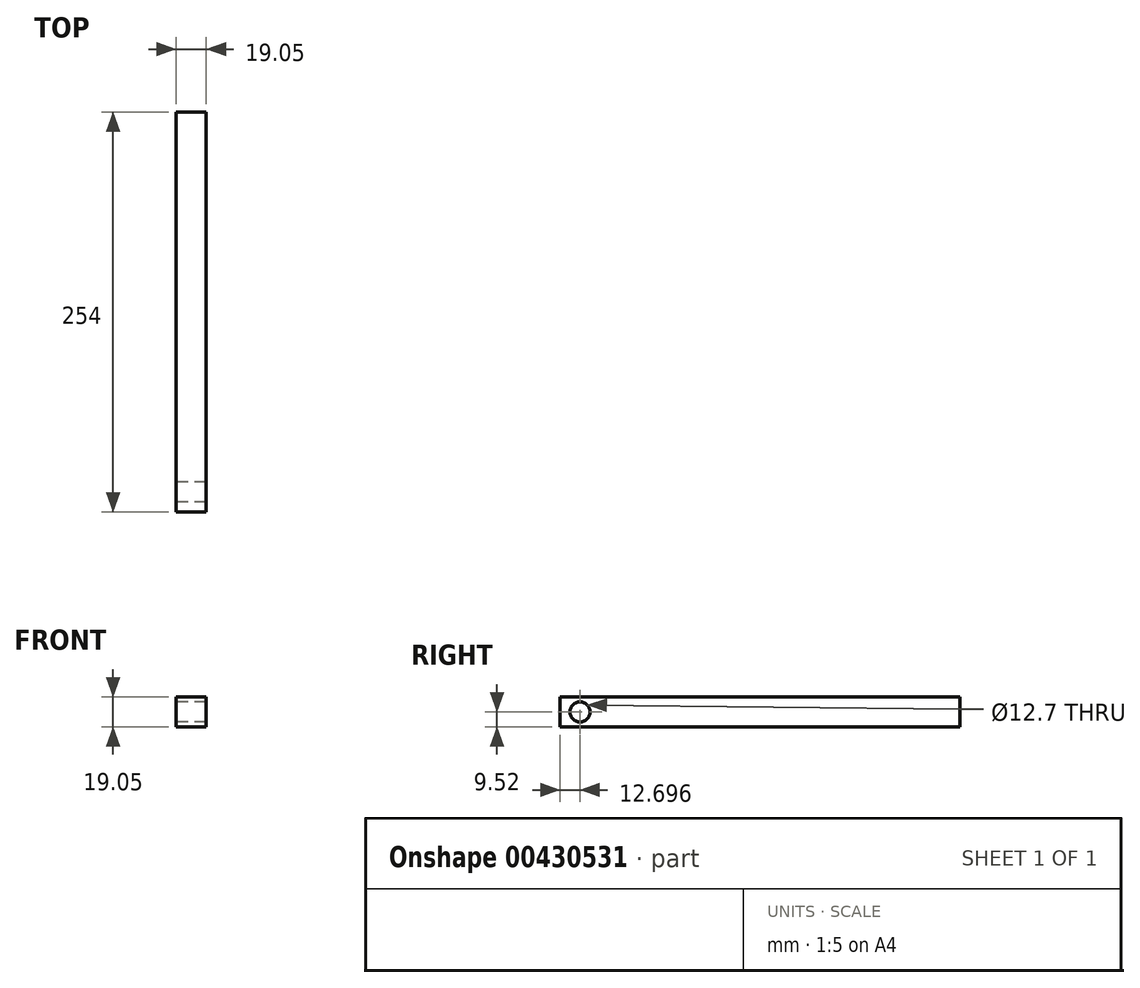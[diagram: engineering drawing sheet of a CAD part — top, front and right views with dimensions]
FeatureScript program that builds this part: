
annotation { "Feature Type Name" : "Feature", "Feature Type Description" : "" }
export const myFeature = defineFeature(function(context is Context, id is Id, definition is map)
    precondition{}
    {
        {
            var Q0;
            Q0=qCreatedBy(makeId("Right.planeOp"),FACE);
            var sketch = newSketch(context, id + "F0", { "sketchPlane" : qUnion([Q0])});
            skLineSegment(sketch, "E0.bottom", {"start": v(-218.13, -39.47) * mm, "end": v(35.87, -39.47) * mm});
            skLineSegment(sketch, "E0.top", {"start": v(-218.13, -58.52) * mm, "end": v(35.87, -58.52) * mm});
            skLineSegment(sketch, "E0.left", {"start": v(-218.13, -39.47) * mm, "end": v(-218.13, -58.52) * mm});
            skLineSegment(sketch, "E0.right", {"start": v(35.87, -39.47) * mm, "end": v(35.87, -58.52) * mm});
            skCircle(sketch, "E1", {"center": v(-205.43, -49) * mm, "radius": 6.35 * mm});
            skSolve(sketch);
        }
        {
            var Q0;
            Q0=makeQuery(id+"F0.imprint","IMPRINT",FACE,{"disambiguationData":[TD([[makeQuery(id+"F0.imprint","IMPRINT",EDGE,{"derivedFrom":sQuery(id+"F0.wireOp",EDGE,"E0.bottom")}),-1.0]])]});
            extrude(context, id + "F1", {"entities" : qUnion([Q0]), "depth" : 19.05 * mm});
        }
    });
